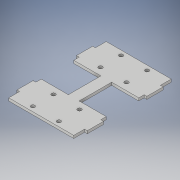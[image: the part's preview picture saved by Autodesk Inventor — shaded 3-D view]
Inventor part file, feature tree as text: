
AUTODESK INVENTOR PART (.ipt)
format: ipt  version: 2019 (Build 230136000, 136)  size: 171,008 bytes
history: native  units: in
note: dims shown in document units (in); Inventor stores cm internally (conversion verified against a paired STEP export)
features: extrude x4, sketch x4
ambient origin geometry x8: Origin, YZ Plane, XZ Plane, XY Plane, X Axis, Y Axis, Z Axis, Center Point
bodies: Solid1 (feature_tree)
feature tree (8):
  extrude  "Extrusion1"  Depth=4.5in
  extrude  "Extrusion2"  Depth=0.75in
  extrude  "Extrusion3"  Depth=0.5in
  extrude  "Extrusion4"  Depth=0.125in
  sketch  "Sketch1"  dims[d0=3.0in d1=4.5in]
  sketch  "Sketch2"  dims[d2=0.125in d3=0.0in d4=0.75in]
  sketch  "Sketch3"  dims[d5=0.75in d6=0.5in]
  sketch  "Sketch4"  dims[d7=0.5in d8=0.125in d9=0.125in d10=0.0in d11=0.125in d12=0.0in d13=0.25in d14=0.25in d15=1.25in d16=0.125in d17=0.0in d24=0.175in d25=0.175in d26=0.175in d27=0.125in d28=0.0in d30=0.95in d33=1.2in d36=1.2in d37=0.9in d38=0.175in]
